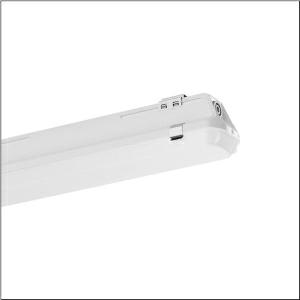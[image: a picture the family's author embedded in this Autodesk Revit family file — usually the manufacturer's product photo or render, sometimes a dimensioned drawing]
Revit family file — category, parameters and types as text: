
# Revit family: monsun_r__11_51fp20dp460h_2810
name_source: partatom
category: Lighting Fixtures
units: mm (PartAtom-declared; Revit-internal decimal feet)

## family parameters
Cut with Voids When Loaded = No
Host = Face
Light Source = No
Part Type = Normal
Room Calculation Point = No
Round Connector Dimension = Use Diameter
Shared = No

## types (1)
- --- (1 x LED, 5450 lm, 34.6 W, 4000K)
    Apparent Load = 35 VA
    CIE Flux Codes = 45 75 93 94 100
    Color Rendering = 80
    Color Temperature = 4000K
    Default Elevation = 1800 mm
    Description = Monsun® 11, damp-proof luminaire, chain hanger, primary optical cover: enclosure, of PC, light emission: direct distribution, primary light characteristic: symmetric, installation type: suspended mounting, surface-mounted, horizontal mounting, vertical mounting, LED, rated luminous flux: 5.450lm, luminous efficacy: 158lm/W, light colour: 840, colour temperature: 4000K, control gear: ECG DALI, with terminal, 5-pole, max. 2.5mm², mains connection: 220..240V, AC, 50/60Hz, rated input power: 35W, luminaire housing, of glass-fibre reinforced polyester, uncoated, bright grey, incl. chain hanger, length: 1.590mm, width: 90mm, height: 88mm, clip for enclosure, of stainless steel (V2A), ceiling mounting element, of stainless steel (V2A), chain hanger, of stainless steel (V2A), protection rating (complete): IP66, insulation class (complete): insulation class I (protective earthing), certification: CE, ENEC, VDE, UKCA, protection symbol: D, impact resistance: IK08, permissible operating ambient temperature: -35..+40°C, standard: EN 50419, EN 60598-2-1, no direct snow, no direct sun, no direct rain, for indoor or canopied outdoor use, corresponds to IFS (International Featured Standards) requirements for safety and quality in the food industry, contact your sales advisor before using the luminaires in applications with unclear chemical exposure, large temperature fluctuations or condensation-forming humidity, LABS conformity tested according to VDMA 24364:2018-05, packaging unit: 1 piece
    Height = 89 mm
    Lamp = 1 x LED
    Lamp Light Flux = 5450 lm
    Lamp Power = 34.6 W
    Lamp count = 1
    Length = 1590 mm
    Luminous efficacy = 158 lm/W
    Manufacturer = Siteco
    ModVariant = No
    Model = 51FP20DP460H
    Mounting Place = Ceiling
    Mounting Type = Surface mounted
    Number of Poles = 1
    OnlyDefault = Yes
    Power Factor = 1
    Product Name = Monsun® 11
    Product group = damp-proof luminaire
    ProductGroupID = 300
    Protection Class = Protection class I
    Protection Degree = IP 66
    RLX_Detail_Level = 1
    RLX_Emergency_Light_Flux = 0 lm
    RLX_Emergency_Type = 0
    RLX_Emergency_Type_DB = No
    RlxData = <blob elided: 92025 chars, md5=22929804>
    Socket = socket
    Standby Power = 0 W
    System Light Flux = 5450 lm
    System Power = 35 W
    Type Comments = factory setting: luminous flux: 100 % | dim-lin: 254 | 232 mA
    Type Image = l_1319650.jpg
    URL = http://relux.com
    VarID = @adj_174145
    Voltage = 0 V
    Weight = 0.00 kg
    Width = 90 mm

## geometry (parser evidence)
native form markers: Blend x4, Sweep x13
no freeform markers — native parametric forms only
